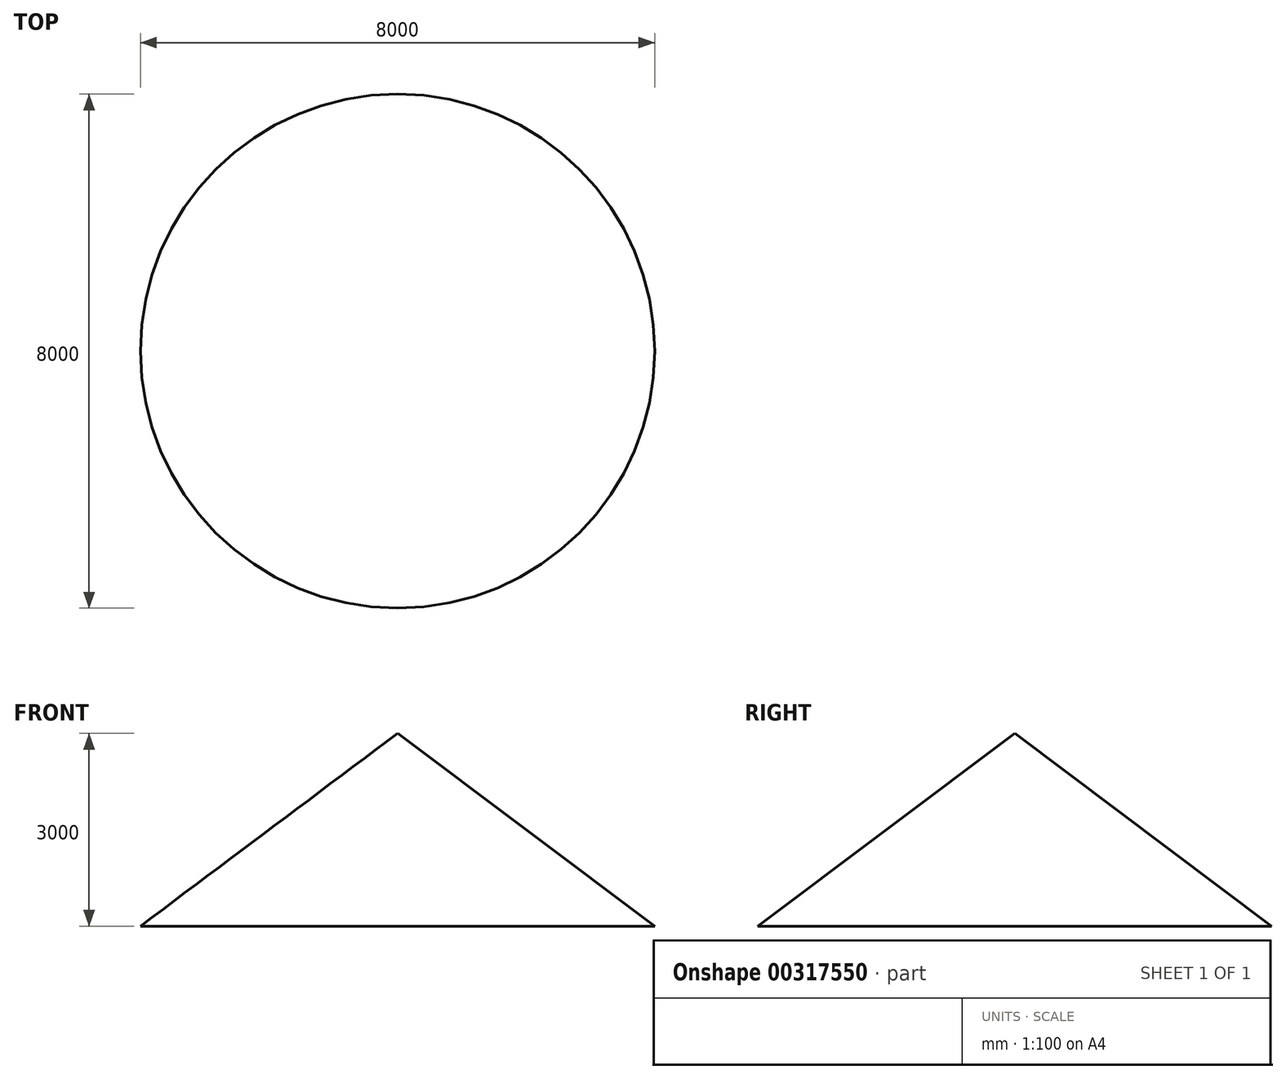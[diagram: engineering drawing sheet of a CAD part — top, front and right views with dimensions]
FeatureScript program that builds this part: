
annotation { "Feature Type Name" : "Feature", "Feature Type Description" : "" }
export const myFeature = defineFeature(function(context is Context, id is Id, definition is map)
    precondition{}
    {
        {
            var Q0;
            Q0=qCreatedBy(makeId("Front.planeOp"),FACE);
            var sketch = newSketch(context, id + "F0", { "sketchPlane" : qUnion([Q0])});
            skLineSegment(sketch, "E0", {"start": v(0, 0) * mm, "end": v(4000, 0) * mm});
            skLineSegment(sketch, "E1", {"start": v(0, 0) * mm, "end": v(0, 3000) * mm});
            skLineSegment(sketch, "E2", {"start": v(0, 3000) * mm, "end": v(4000, 0) * mm});
            skLineSegment(sketch, "E3", {"start": v(0, 3245.36) * mm, "end": v(0, -246.5) * mm, "construction": true});
            skSolve(sketch);
        }
        {
            var Q0;
            Q0=makeQuery(id+"F0.imprint","IMPRINT",FACE,{"disambiguationData":[TD([[makeQuery(id+"F0.imprint","IMPRINT",EDGE,{"derivedFrom":sQuery(id+"F0.wireOp",EDGE,"E0")}),1.0]])]});
            var Q1;
            Q1=sQuery(id+"F0.wireOp",EDGE,"E3");
            revolve(context, id + "F1", {"entities" : qUnion([Q0]), "axis" : qUnion([Q1]), "revolveType" : RevolveType.FULL});
        }
    });
